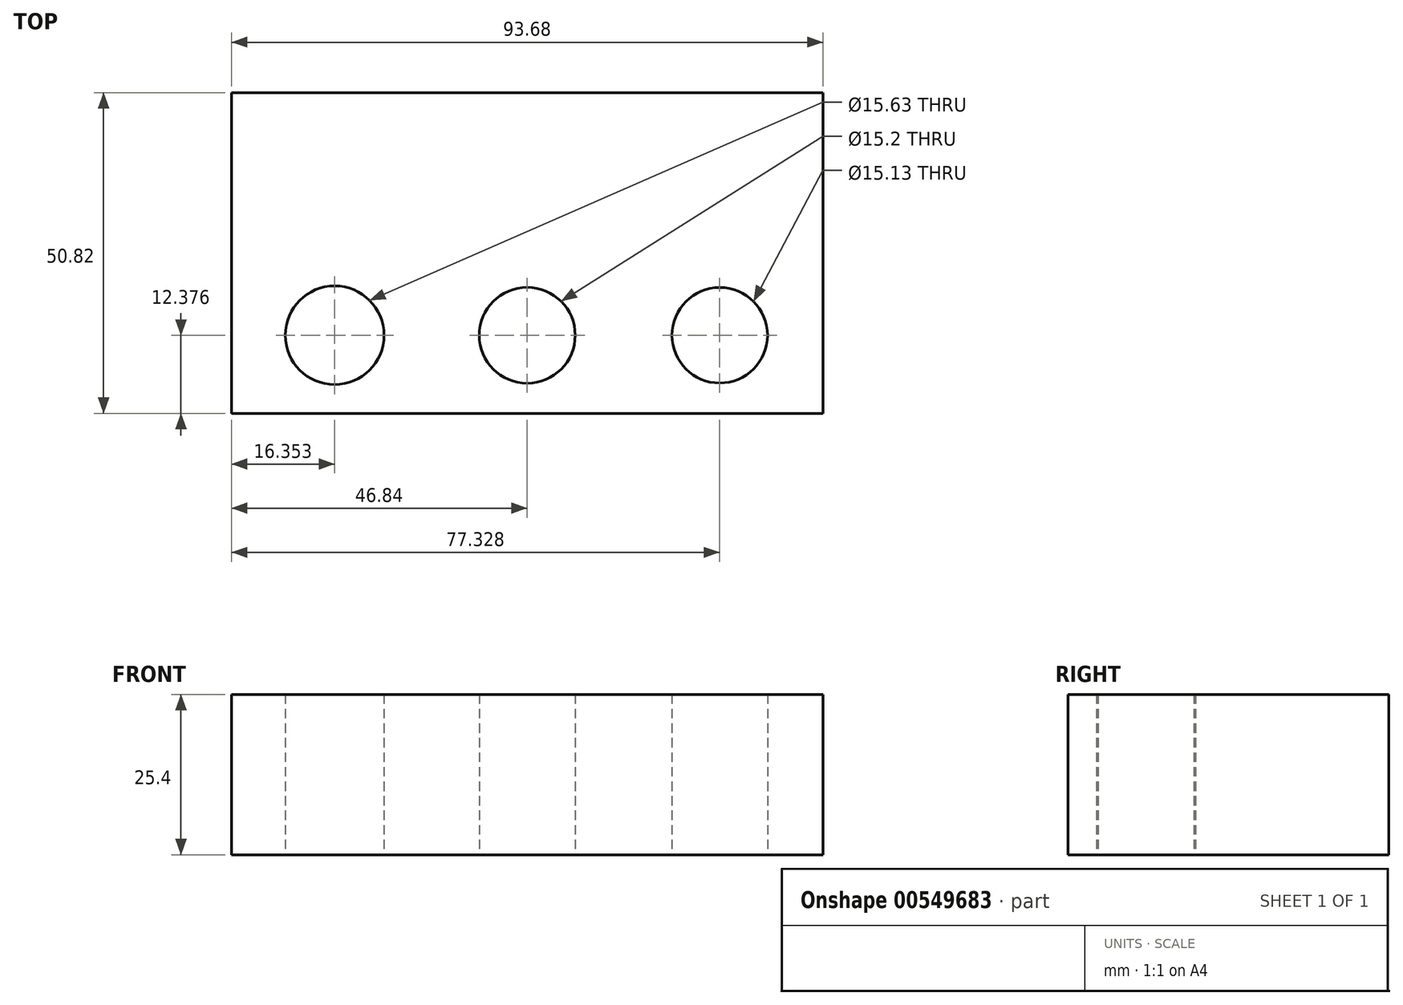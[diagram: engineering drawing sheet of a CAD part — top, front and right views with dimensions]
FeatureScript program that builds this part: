
annotation { "Feature Type Name" : "Feature", "Feature Type Description" : "" }
export const myFeature = defineFeature(function(context is Context, id is Id, definition is map)
    precondition{}
    {
        {
            var Q0;
            Q0=qCreatedBy(makeId("Top.planeOp"),FACE);
            var sketch = newSketch(context, id + "F0", { "sketchPlane" : qUnion([Q0])});
            skLineSegment(sketch, "E0.bottom", {"start": v(-46.84, 25.4) * mm, "end": v(46.84, 25.4) * mm});
            skLineSegment(sketch, "E0.top", {"start": v(-46.84, -25.4) * mm, "end": v(46.84, -25.4) * mm});
            skLineSegment(sketch, "E0.left", {"start": v(-46.84, 25.4) * mm, "end": v(-46.84, -25.4) * mm});
            skLineSegment(sketch, "E0.right", {"start": v(46.84, 25.4) * mm, "end": v(46.84, -25.4) * mm});
            skPoint(sketch, "E0.middle", {"position": v(0, 0) * mm});
            skCircle(sketch, "E1", {"center": v(-30.49, 13.03) * mm, "radius": 7.82 * mm});
            skCircle(sketch, "E2", {"center": v(0, 13.03) * mm, "radius": 7.6 * mm});
            skCircle(sketch, "E3", {"center": v(30.49, 13.03) * mm, "radius": 7.56 * mm});
            skCircle(sketch, "E4.MirrorC", {"center": v(-30.49, -13.03) * mm, "radius": 7.82 * mm});
            skCircle(sketch, "E5.MirrorC", {"center": v(0, -13.03) * mm, "radius": 7.6 * mm});
            skCircle(sketch, "E6.MirrorC", {"center": v(30.49, -13.03) * mm, "radius": 7.56 * mm});
            skSolve(sketch);
        }
        {
            var Q0;
            Q0=makeQuery(id+"F0.imprint","IMPRINT",FACE,{"disambiguationData":[TD([[makeQuery(id+"F0.imprint","IMPRINT",EDGE,{"derivedFrom":sQuery(id+"F0.wireOp",EDGE,"E6.MirrorC")}),-1.0]])]});
            var Q1;
            Q1=makeQuery(id+"F0.imprint","IMPRINT",FACE,{"disambiguationData":[TD([[makeQuery(id+"F0.imprint","IMPRINT",EDGE,{"derivedFrom":sQuery(id+"F0.wireOp",EDGE,"E5.MirrorC")}),-1.0]])]});
            var Q2;
            Q2=makeQuery(id+"F0.imprint","IMPRINT",FACE,{"disambiguationData":[TD([[makeQuery(id+"F0.imprint","IMPRINT",EDGE,{"derivedFrom":sQuery(id+"F0.wireOp",EDGE,"E4.MirrorC")}),-1.0]])]});
            var Q3;
            Q3=makeQuery(id+"F0.imprint","IMPRINT",FACE,{"disambiguationData":[TD([[makeQuery(id+"F0.imprint","IMPRINT",EDGE,{"derivedFrom":sQuery(id+"F0.wireOp",EDGE,"E1")}),1.0]])]});
            var Q4;
            Q4=makeQuery(id+"F0.imprint","IMPRINT",FACE,{"disambiguationData":[TD([[makeQuery(id+"F0.imprint","IMPRINT",EDGE,{"derivedFrom":sQuery(id+"F0.wireOp",EDGE,"E2")}),1.0]])]});
            var Q5;
            Q5=makeQuery(id+"F0.imprint","IMPRINT",FACE,{"disambiguationData":[TD([[makeQuery(id+"F0.imprint","IMPRINT",EDGE,{"derivedFrom":sQuery(id+"F0.wireOp",EDGE,"E3")}),1.0]])]});
            extrude(context, id + "F1", {"entities" : qUnion([Q0, Q1, Q2, Q3, Q4, Q5]), "depth" : 25.4 * mm, "offsetDistance" : 25.4 * mm});
        }
    });
